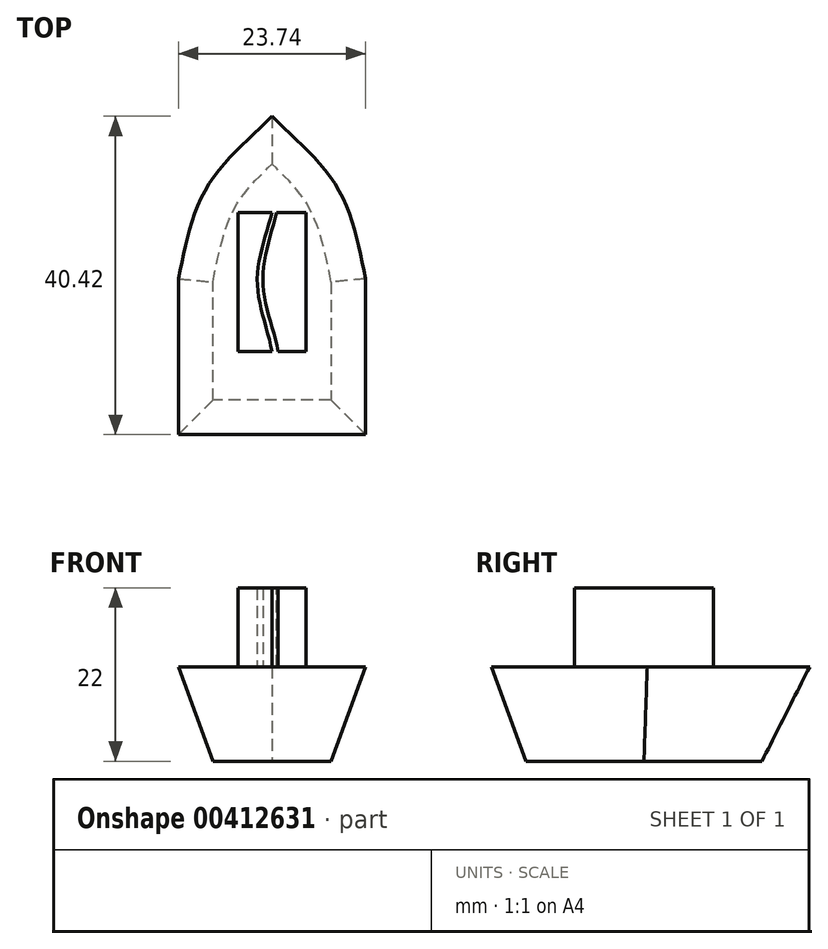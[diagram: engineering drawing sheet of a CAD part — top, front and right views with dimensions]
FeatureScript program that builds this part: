
annotation { "Feature Type Name" : "Feature", "Feature Type Description" : "" }
export const myFeature = defineFeature(function(context is Context, id is Id, definition is map)
    precondition{}
    {
        {
            var Q0;
            Q0=qCreatedBy(makeId("Top.planeOp"),FACE);
            var sketch = newSketch(context, id + "F0", { "sketchPlane" : qUnion([Q0])});
            skLineSegment(sketch, "E0.top", {"start": v(7.5, -15) * mm, "end": v(-7.5, -15) * mm});
            skLineSegment(sketch, "E0.left", {"start": v(7.5, 0) * mm, "end": v(7.5, -15) * mm});
            skLineSegment(sketch, "E0.right", {"start": v(-7.5, 0) * mm, "end": v(-7.5, -15) * mm});
            skPoint(sketch, "E0.middle", {"position": v(0, 0) * mm});
            skFitSpline(sketch, "E1", {"points": [v(-7.5, 0) * mm, v(-4.81, 9.26) * mm, v(0, 15) * mm], "startDerivative": vector(3.67, 18.8) * mm, "endDerivative": vector(11.5, 11.04) * mm});
            skFitSpline(sketch, "E2.MirrorCS", {"points": [v(7.5, 0) * mm, v(4.81, 9.26) * mm, v(0, 15) * mm], "startDerivative": vector(-3.67, 18.8) * mm, "endDerivative": vector(-11.5, 11.04) * mm});
            skPoint(sketch, "E3.orphan", {"position": v(7.5, 15) * mm});
            skPoint(sketch, "E4.orphan", {"position": v(-7.5, 15) * mm});
            skSolve(sketch);
        }
        {
            var Q0;
            Q0=makeQuery(id+"F0.imprint","IMPRINT",FACE,{"disambiguationData":[TD([[makeQuery(id+"F0.imprint","IMPRINT",EDGE,{"derivedFrom":sQuery(id+"F0.wireOp",EDGE,"E0.top")}),-1.0]])]});
            extrude(context, id + "F1", {"entities" : qUnion([Q0]), "depth" : 12 * mm, "hasDraft" : true, "draftAngle" : 20 * degree});
        }
        {
            var Q0;
            Q0=makeQuery(id+"F1.opExtrude","CAP_FACE",FACE,{"disambiguationData":[OSD([sQuery(id+"F0.wireOp",EDGE,"E0.top"),sQuery(id+"F0.wireOp",EDGE,"E0.left"),sQuery(id+"F0.wireOp",EDGE,"E0.right"),sQuery(id+"F0.wireOp",EDGE,"E1"),sQuery(id+"F0.wireOp",EDGE,"E2.MirrorCS")])],"isStart":false});
            var sketch = newSketch(context, id + "F2", { "sketchPlane" : qUnion([Q0])});
            skLineSegment(sketch, "E5.bottom", {"start": v(4.32, -8.83) * mm, "end": v(-4.32, -8.83) * mm});
            skLineSegment(sketch, "E5.top", {"start": v(4.32, 8.83) * mm, "end": v(-4.32, 8.83) * mm});
            skLineSegment(sketch, "E5.left", {"start": v(4.32, -8.83) * mm, "end": v(4.32, 8.83) * mm});
            skLineSegment(sketch, "E5.right", {"start": v(-4.32, -8.83) * mm, "end": v(-4.32, 8.83) * mm});
            skPoint(sketch, "E5.middle", {"position": v(0, 0) * mm});
            skSolve(sketch);
        }
        {
            var Q0;
            Q0 = qSketchRegion(id + "F2", true);
            extrude(context, id + "F3", {"entities" : qUnion([Q0]), "operationType" : NewBodyOperationType.ADD, "depth" : 10 * mm});
        }
        {
            var Q0;
            Q0=makeQuery(id+"F3.opExtrude","CAP_FACE",FACE,{"disambiguationData":[OSD([sQuery(id+"F2.wireOp",EDGE,"E5.bottom"),sQuery(id+"F2.wireOp",EDGE,"E5.top"),sQuery(id+"F2.wireOp",EDGE,"E5.left"),sQuery(id+"F2.wireOp",EDGE,"E5.right")])],"isStart":false});
            var sketch = newSketch(context, id + "F4", { "sketchPlane" : qUnion([Q0])});
            skFitSpline(sketch, "E6", {"points": [v(0, -8.83) * mm, v(-1.87, 0) * mm, v(0, 8.83) * mm], "startDerivative": vector(-3.37, 17.72) * mm, "endDerivative": vector(4.63, 17.58) * mm});
            skFitSpline(sketch, "E7", {"points": [v(0.79, -8.83) * mm, v(-1.16, 0) * mm, v(0.58, 8.83) * mm], "startDerivative": vector(-3.46, 17.7) * mm, "endDerivative": vector(4.6, 17.6) * mm});
            skLineSegment(sketch, "E8", {"start": v(0.58, 8.83) * mm, "end": v(0, 8.83) * mm});
            skLineSegment(sketch, "E9", {"start": v(0.79, -8.83) * mm, "end": v(0, -8.83) * mm});
            skSolve(sketch);
        }
        {
            var Q0;
            Q0 = qSketchRegion(id + "F4", true);
            var Q1;
            Q1=makeQuery(id+"F1.opExtrude","CAP_FACE",FACE,{"disambiguationData":[OSD([sQuery(id+"F0.wireOp",EDGE,"E0.top"),sQuery(id+"F0.wireOp",EDGE,"E0.left"),sQuery(id+"F0.wireOp",EDGE,"E0.right"),sQuery(id+"F0.wireOp",EDGE,"E1"),sQuery(id+"F0.wireOp",EDGE,"E2.MirrorCS")])],"isStart":false});
            extrude(context, id + "F5", {"entities" : qUnion([Q0]), "operationType" : NewBodyOperationType.REMOVE, "endBound" : BoundingType.UP_TO_SURFACE, "oppositeDirection" : true, "endBoundEntityFace" : qUnion([Q1]), "depth" : 25 * mm});
        }
    });
